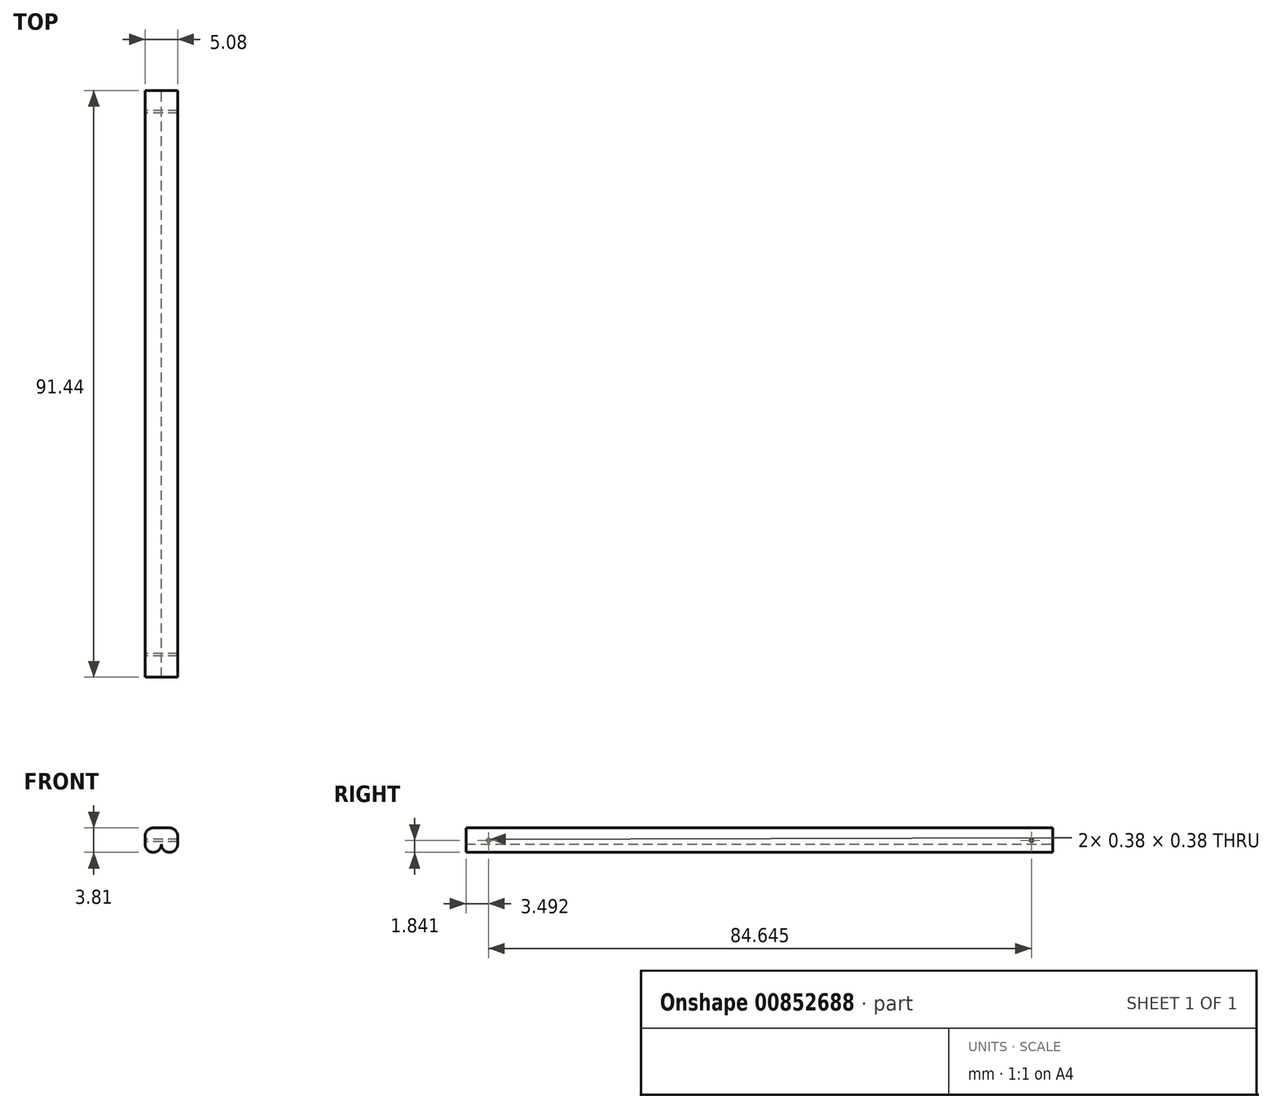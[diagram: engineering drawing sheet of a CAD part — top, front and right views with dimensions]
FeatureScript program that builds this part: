
annotation { "Feature Type Name" : "Feature", "Feature Type Description" : "" }
export const myFeature = defineFeature(function(context is Context, id is Id, definition is map)
    precondition{}
    {
        {
            var Q0;
            Q0=qCreatedBy(makeId("Front.planeOp"),FACE);
            var sketch = newSketch(context, id + "F0", { "sketchPlane" : qUnion([Q0])});
            skLineSegment(sketch, "E0.bottom", {"start": v(-2.54, 1.27) * mm, "end": v(2.54, 1.27) * mm});
            skLineSegment(sketch, "E0.left", {"start": v(-2.54, 1.27) * mm, "end": v(-2.54, -1.27) * mm});
            skLineSegment(sketch, "E0.right", {"start": v(2.54, 1.27) * mm, "end": v(2.54, -1.27) * mm});
            skPoint(sketch, "E0.middle", {"position": v(0, 0) * mm});
            skArc(sketch, "E1", {"start": v(-2.54, -1.27) * mm, "mid": v(-1.27, -2.54) * mm, "end": v(0, -1.27) * mm});
            skPoint(sketch, "E1.second.point", {"position": v(0, -1.27) * mm});
            skPoint(sketch, "E1.third.point", {"position": v(-1.27, 0) * mm});
            skArc(sketch, "E2.MirrorC", {"start": v(2.54, -1.27) * mm, "mid": v(1.27, -2.54) * mm, "end": v(0, -1.27) * mm});
            skPoint(sketch, "E3.trimOffspring.end.orphan", {"position": v(2.54, 0) * mm});
            skSolve(sketch);
        }
        {
            var Q0;
            Q0=makeQuery(id+"F0.imprint","IMPRINT",FACE,{"disambiguationData":[TD([[makeQuery(id+"F0.imprint","IMPRINT",EDGE,{"derivedFrom":sQuery(id+"F0.wireOp",EDGE,"E0.bottom")}),-1.0]])]});
            extrude(context, id + "F1", {"entities" : qUnion([Q0]), "depth" : 91.44 * mm, "offsetDistance" : 25.4 * mm});
        }
        {
            var Q0;
            Q0=makeQuery(id+"F1.opExtrude","SWEPT_EDGE",EDGE,{"disambiguationData":[OSD([sQuery(id+"F0.wireOp",EDGE,"E0.bottom"),sQuery(id+"F0.wireOp",EDGE,"E0.right")])]});
            var Q1;
            Q1=makeQuery(id+"F1.opExtrude","SWEPT_EDGE",EDGE,{"disambiguationData":[OSD([sQuery(id+"F0.wireOp",EDGE,"E0.bottom"),sQuery(id+"F0.wireOp",EDGE,"E0.left")])]});
            fillet(context, id + "F2", {"entities" : qUnion([Q0, Q1]), "radius" : 1.27 * mm, "tangentPropagation" : true, "allowEdgeOverflow" : false});
        }
        {
            var Q0;
            Q0=makeQuery(id+"F1.opExtrude","SWEPT_FACE",FACE,{"disambiguationData":[OSD([sQuery(id+"F0.wireOp",EDGE,"E0.left")])]});
            var sketch = newSketch(context, id + "F3", { "sketchPlane" : qUnion([Q0])});
            skLineSegment(sketch, "E4.bottom", {"start": v(3.11, -0.5) * mm, "end": v(3.5, -0.5) * mm});
            skLineSegment(sketch, "E4.top", {"start": v(3.11, -0.88) * mm, "end": v(3.5, -0.88) * mm});
            skLineSegment(sketch, "E4.left", {"start": v(3.11, -0.5) * mm, "end": v(3.11, -0.88) * mm});
            skLineSegment(sketch, "E4.right", {"start": v(3.5, -0.5) * mm, "end": v(3.5, -0.88) * mm});
            skPoint(sketch, "E4.middle", {"position": v(3.3, -0.7) * mm});
            skLineSegment(sketch, "E5.bottom", {"start": v(87.76, -0.5) * mm, "end": v(88.14, -0.5) * mm});
            skLineSegment(sketch, "E5.top", {"start": v(87.76, -0.89) * mm, "end": v(88.14, -0.89) * mm});
            skLineSegment(sketch, "E5.left", {"start": v(87.76, -0.5) * mm, "end": v(87.76, -0.89) * mm});
            skLineSegment(sketch, "E5.right", {"start": v(88.14, -0.5) * mm, "end": v(88.14, -0.89) * mm});
            skPoint(sketch, "E5.middle", {"position": v(87.95, -0.7) * mm});
            skSolve(sketch);
        }
        {
            var Q0;
            Q0=makeQuery(id+"F3.imprint","IMPRINT",FACE,{"disambiguationData":[TD([[makeQuery(id+"F3.imprint","IMPRINT",EDGE,{"derivedFrom":sQuery(id+"F3.wireOp",EDGE,"E4.bottom")}),-1.0]])]});
            extrude(context, id + "F4", {"entities" : qUnion([Q0]), "operationType" : NewBodyOperationType.REMOVE, "endBound" : BoundingType.THROUGH_ALL, "oppositeDirection" : true, "depth" : 25.4 * mm, "offsetDistance" : 25.4 * mm});
        }
        {
            var Q0;
            Q0=makeQuery(id+"F3.imprint","IMPRINT",FACE,{"disambiguationData":[TD([[makeQuery(id+"F3.imprint","IMPRINT",EDGE,{"derivedFrom":sQuery(id+"F3.wireOp",EDGE,"E5.bottom")}),-1.0]])]});
            extrude(context, id + "F5", {"entities" : qUnion([Q0]), "operationType" : NewBodyOperationType.REMOVE, "endBound" : BoundingType.THROUGH_ALL, "oppositeDirection" : true, "depth" : 25.4 * mm, "offsetDistance" : 25.4 * mm});
        }
    });
